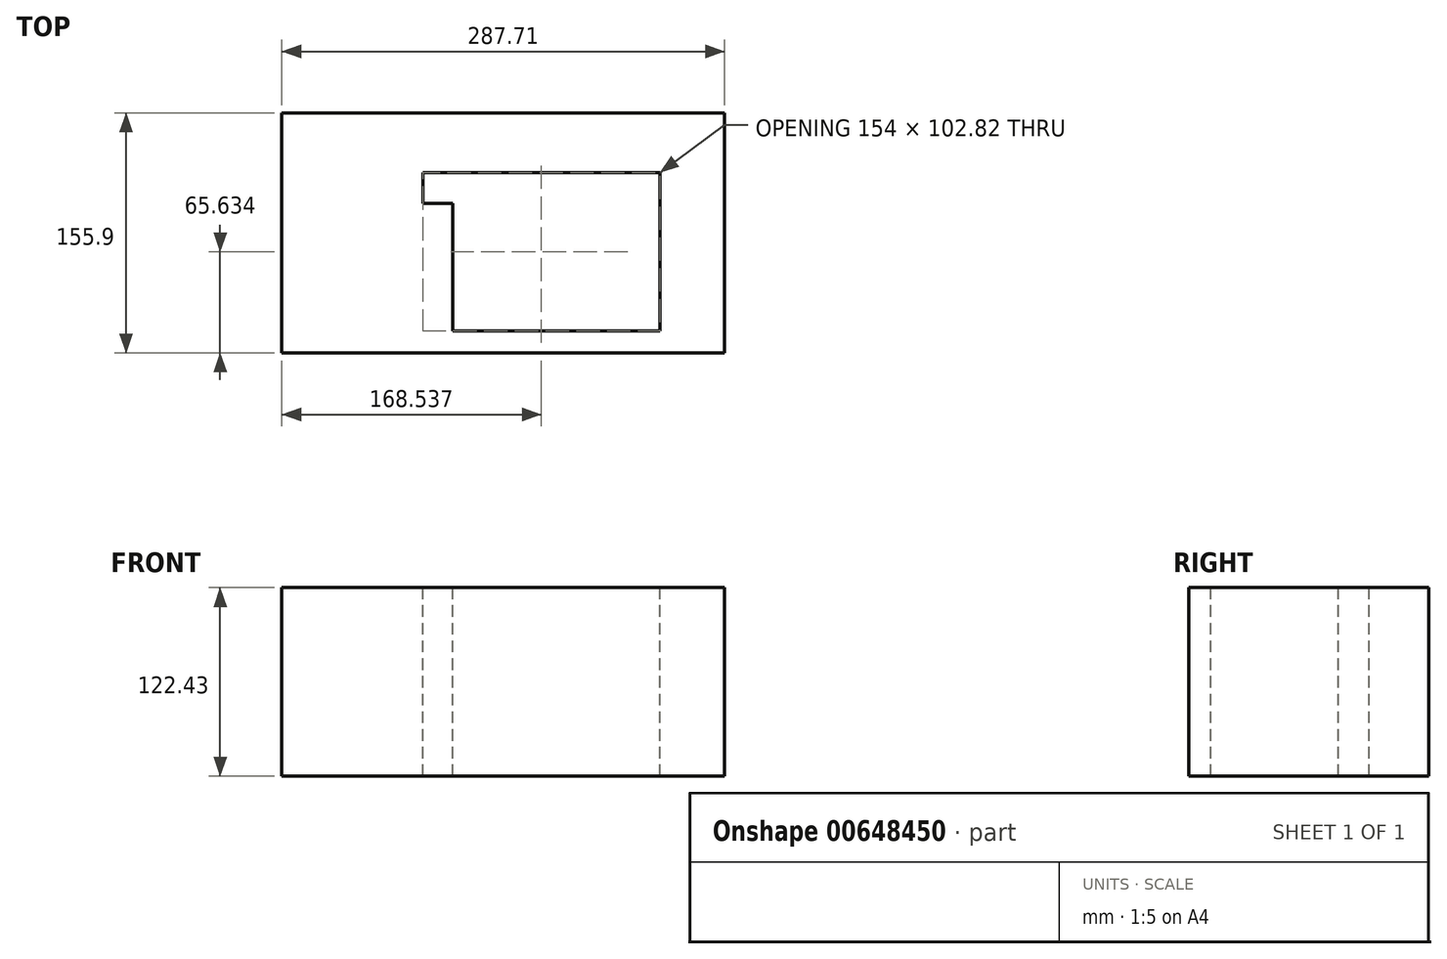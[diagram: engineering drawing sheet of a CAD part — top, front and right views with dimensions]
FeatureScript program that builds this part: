
annotation { "Feature Type Name" : "Feature", "Feature Type Description" : "" }
export const myFeature = defineFeature(function(context is Context, id is Id, definition is map)
    precondition{}
    {
        {
            var Q0;
            Q0=qCreatedBy(makeId("Top.planeOp"),FACE);
            var sketch = newSketch(context, id + "F0", { "sketchPlane" : qUnion([Q0])});
            skLineSegment(sketch, "E0.bottom", {"start": v(145.3, -80.46) * mm, "end": v(-142.4, -80.46) * mm});
            skLineSegment(sketch, "E0.top", {"start": v(145.3, 75.44) * mm, "end": v(-142.4, 75.44) * mm});
            skLineSegment(sketch, "E0.left", {"start": v(145.3, -80.46) * mm, "end": v(145.3, 75.44) * mm});
            skLineSegment(sketch, "E0.right", {"start": v(-142.4, -80.46) * mm, "end": v(-142.4, 75.44) * mm});
            skLineSegment(sketch, "E1.bottom", {"start": v(0, 0) * mm, "end": v(-24.5, 0) * mm});
            skLineSegment(sketch, "E1.top", {"start": v(0, 16.62) * mm, "end": v(-24.5, 16.62) * mm});
            skLineSegment(sketch, "E1.left", {"start": v(0, 0) * mm, "end": v(0, 16.62) * mm});
            skLineSegment(sketch, "E1.right", {"start": v(-24.5, 0) * mm, "end": v(-24.5, 16.62) * mm});
            skLineSegment(sketch, "E2.bottom", {"start": v(-50.87, 16.62) * mm, "end": v(-31.34, 16.62) * mm});
            skLineSegment(sketch, "E2.top", {"start": v(-50.87, 36.59) * mm, "end": v(-31.34, 36.59) * mm});
            skLineSegment(sketch, "E2.left", {"start": v(-50.87, 16.62) * mm, "end": v(-50.87, 36.59) * mm});
            skLineSegment(sketch, "E2.right", {"start": v(-31.34, 16.62) * mm, "end": v(-31.34, 36.59) * mm});
            skLineSegment(sketch, "E3.bottom", {"start": v(-31.34, 36.59) * mm, "end": v(103.13, 36.59) * mm});
            skLineSegment(sketch, "E3.top", {"start": v(-31.34, -66.24) * mm, "end": v(103.13, -66.24) * mm});
            skLineSegment(sketch, "E3.left", {"start": v(-31.34, 36.59) * mm, "end": v(-31.34, -66.24) * mm});
            skLineSegment(sketch, "E3.right", {"start": v(103.13, 36.59) * mm, "end": v(103.13, -66.24) * mm});
            skSolve(sketch);
        }
        {
            var Q0;
            Q0 = qSketchRegion(id + "F0", true);
            extrude(context, id + "F1", {"entities" : qUnion([Q0]), "oppositeDirection" : true, "depth" : 122.43 * mm, "offsetDistance" : 25.4 * mm});
        }
    });
